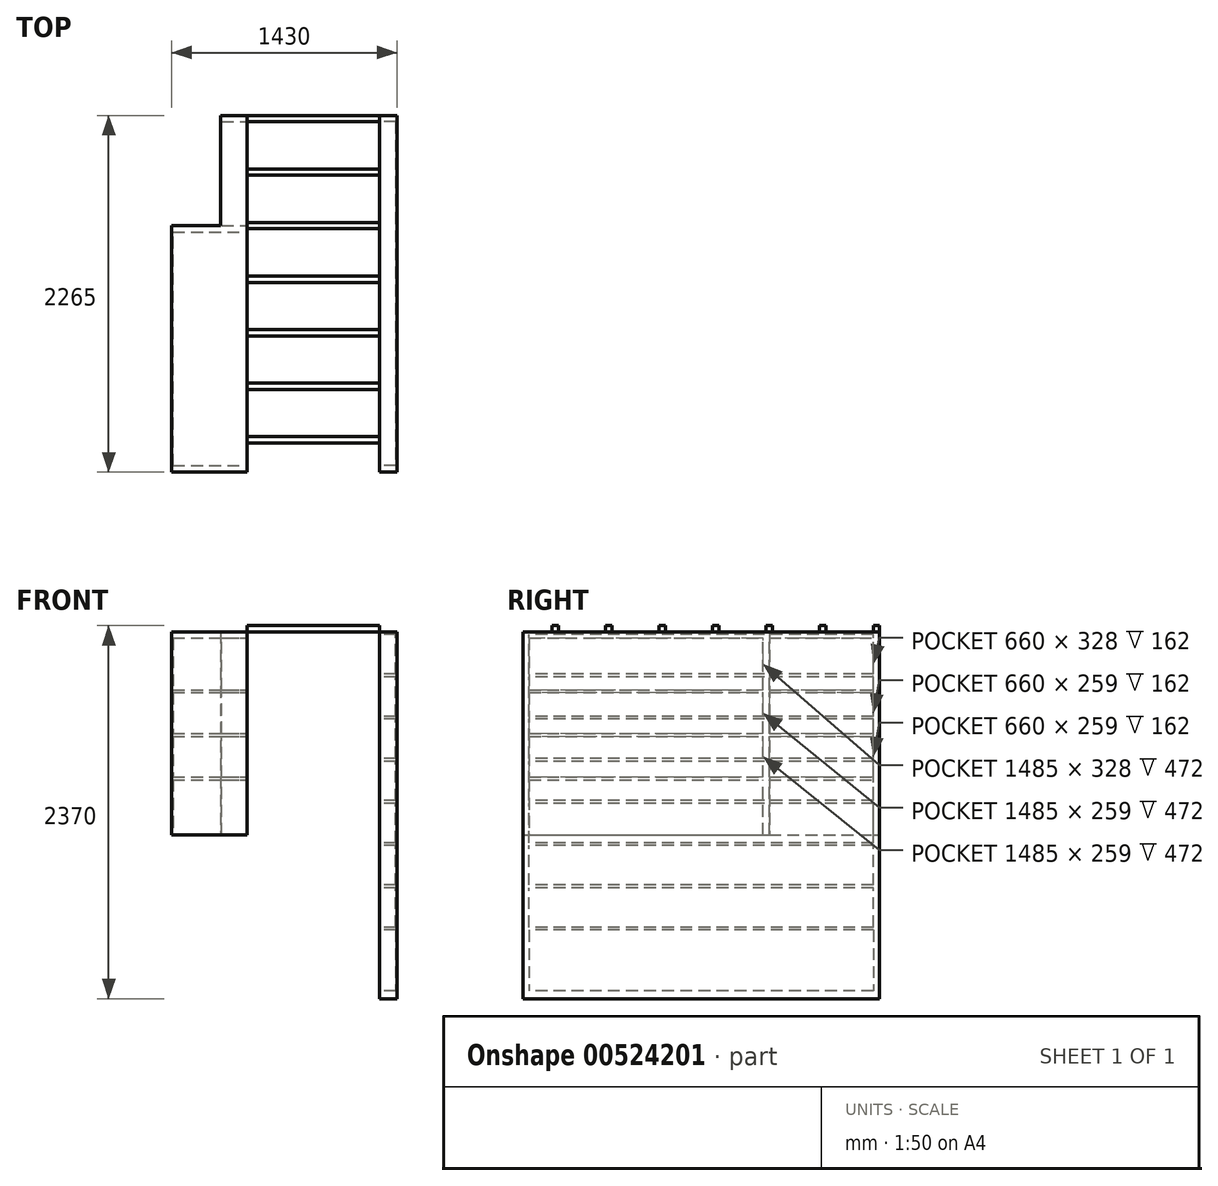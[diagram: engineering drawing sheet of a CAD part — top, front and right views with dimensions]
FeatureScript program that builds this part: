
annotation { "Feature Type Name" : "Feature", "Feature Type Description" : "" }
export const myFeature = defineFeature(function(context is Context, id is Id, definition is map)
    precondition{}
    {
        {
            var Q0;
            Q0=qCreatedBy(makeId("Top.planeOp"),FACE);
            var sketch = newSketch(context, id + "F0", { "sketchPlane" : qUnion([Q0])});
            skLineSegment(sketch, "E0.bottom", {"start": v(0, 0) * mm, "end": v(-110, 0) * mm});
            skLineSegment(sketch, "E0.left", {"start": v(0, 0) * mm, "end": v(0, 789.64) * mm});
            skLineSegment(sketch, "E0.right", {"start": v(-110, 0) * mm, "end": v(-110, 789.64) * mm});
            skLineSegment(sketch, "E1.bottom", {"start": v(-1120, 2265) * mm, "end": v(-950, 2265) * mm});
            skLineSegment(sketch, "E1.top", {"start": v(-1120, 0) * mm, "end": v(-950, 0) * mm});
            skLineSegment(sketch, "E1.left", {"start": v(-1120, 2265) * mm, "end": v(-1120, 1565) * mm});
            skLineSegment(sketch, "E1.right", {"start": v(-950, 2265) * mm, "end": v(-950, 0) * mm});
            skLineSegment(sketch, "E2.bottom", {"start": v(-1120, 1565) * mm, "end": v(-1430, 1565) * mm});
            skLineSegment(sketch, "E2.top", {"start": v(-950, 0) * mm, "end": v(-1430, 0) * mm});
            skLineSegment(sketch, "E2.right", {"start": v(-1430, 1565) * mm, "end": v(-1430, 0) * mm});
            skLineSegment(sketch, "E3.bottom", {"start": v(-110, 2265) * mm, "end": v(0, 2265) * mm});
            skLineSegment(sketch, "E3.top", {"start": v(-110, 0) * mm, "end": v(0, 0) * mm});
            skLineSegment(sketch, "E3.left", {"start": v(-110, 2265) * mm, "end": v(-110, 0) * mm});
            skLineSegment(sketch, "E3.right", {"start": v(0, 2265) * mm, "end": v(0, 0) * mm});
            skSolve(sketch);
        }
        {
            var Q0;
            Q0 = qSketchRegion(id + "F0", true);
            extrude(context, id + "F1", {"entities" : qUnion([Q0]), "depth" : 2330 * mm, "offsetDistance" : 25 * mm});
        }
        {
            var Q0;
            Q0=makeQuery(id+"F1.opExtrude","SWEPT_FACE",FACE,{"disambiguationData":[OSD([sQuery(id+"F0.wireOp",EDGE,"E3.left")])]});
            var sketch = newSketch(context, id + "F2", { "sketchPlane" : qUnion([Q0])});
            skLineSegment(sketch, "E4.0", {"start": v(-2265, 2330) * mm, "end": v(-2265, 0) * mm});
            skLineSegment(sketch, "E5.0", {"start": v(0, 2330) * mm, "end": v(0, 0) * mm});
            skLineSegment(sketch, "E6.0", {"start": v(-2265, 2330) * mm, "end": v(0, 2330) * mm});
            skLineSegment(sketch, "E7.0", {"start": v(-2265, 0) * mm, "end": v(0, 0) * mm});
            skLineSegment(sketch, "E8.bottom", {"start": v(-2225, 436) * mm, "end": v(-40, 436) * mm});
            skLineSegment(sketch, "E8.top", {"start": v(-2225, 50) * mm, "end": v(-40, 50) * mm});
            skLineSegment(sketch, "E8.left", {"start": v(-2225, 436) * mm, "end": v(-2225, 50) * mm});
            skLineSegment(sketch, "E8.right", {"start": v(-40, 436) * mm, "end": v(-40, 50) * mm});
            skLineSegment(sketch, "E9.bottom", {"start": v(-2225, 454) * mm, "end": v(-40, 454) * mm});
            skLineSegment(sketch, "E9.top", {"start": v(-2225, 704) * mm, "end": v(-40, 704) * mm});
            skLineSegment(sketch, "E9.left", {"start": v(-2225, 454) * mm, "end": v(-2225, 704) * mm});
            skLineSegment(sketch, "E9.right", {"start": v(-40, 454) * mm, "end": v(-40, 704) * mm});
            skLineSegment(sketch, "E10.bottom", {"start": v(-2225, 722) * mm, "end": v(-40, 722) * mm});
            skLineSegment(sketch, "E10.top", {"start": v(-2225, 972) * mm, "end": v(-40, 972) * mm});
            skLineSegment(sketch, "E10.left", {"start": v(-2225, 722) * mm, "end": v(-2225, 972) * mm});
            skLineSegment(sketch, "E10.right", {"start": v(-40, 722) * mm, "end": v(-40, 972) * mm});
            skLineSegment(sketch, "E11.bottom", {"start": v(-2225, 990) * mm, "end": v(-40, 990) * mm});
            skLineSegment(sketch, "E11.top", {"start": v(-2225, 1240) * mm, "end": v(-40, 1240) * mm});
            skLineSegment(sketch, "E11.left", {"start": v(-2225, 990) * mm, "end": v(-2225, 1240) * mm});
            skLineSegment(sketch, "E11.right", {"start": v(-40, 990) * mm, "end": v(-40, 1240) * mm});
            skLineSegment(sketch, "E12.bottom", {"start": v(-2225, 1258) * mm, "end": v(-40, 1258) * mm});
            skLineSegment(sketch, "E12.top", {"start": v(-2225, 1508) * mm, "end": v(-40, 1508) * mm});
            skLineSegment(sketch, "E12.left", {"start": v(-2225, 1258) * mm, "end": v(-2225, 1508) * mm});
            skLineSegment(sketch, "E12.right", {"start": v(-40, 1258) * mm, "end": v(-40, 1508) * mm});
            skLineSegment(sketch, "E13.bottom", {"start": v(-2225, 1526) * mm, "end": v(-40, 1526) * mm});
            skLineSegment(sketch, "E13.top", {"start": v(-2225, 1776) * mm, "end": v(-40, 1776) * mm});
            skLineSegment(sketch, "E13.left", {"start": v(-2225, 1526) * mm, "end": v(-2225, 1776) * mm});
            skLineSegment(sketch, "E13.right", {"start": v(-40, 1526) * mm, "end": v(-40, 1776) * mm});
            skLineSegment(sketch, "E14.bottom", {"start": v(-2225, 1794) * mm, "end": v(-40, 1794) * mm});
            skLineSegment(sketch, "E14.top", {"start": v(-2225, 2044) * mm, "end": v(-40, 2044) * mm});
            skLineSegment(sketch, "E14.left", {"start": v(-2225, 1794) * mm, "end": v(-2225, 2044) * mm});
            skLineSegment(sketch, "E14.right", {"start": v(-40, 1794) * mm, "end": v(-40, 2044) * mm});
            skLineSegment(sketch, "E15.bottom", {"start": v(-2225, 2062) * mm, "end": v(-40, 2062) * mm});
            skLineSegment(sketch, "E15.top", {"start": v(-2225, 2312) * mm, "end": v(-40, 2312) * mm});
            skLineSegment(sketch, "E15.left", {"start": v(-2225, 2062) * mm, "end": v(-2225, 2312) * mm});
            skLineSegment(sketch, "E15.right", {"start": v(-40, 2062) * mm, "end": v(-40, 2312) * mm});
            skSolve(sketch);
        }
        {
            var Q0;
            Q0=makeQuery(id+"F2.imprint","IMPRINT",FACE,{"disambiguationData":[TD([[makeQuery(id+"F2.imprint","IMPRINT",EDGE,{"derivedFrom":sQuery(id+"F2.wireOp",EDGE,"E15.bottom")}),1.0]])]});
            var Q1;
            Q1=makeQuery(id+"F2.imprint","IMPRINT",FACE,{"disambiguationData":[TD([[makeQuery(id+"F2.imprint","IMPRINT",EDGE,{"derivedFrom":sQuery(id+"F2.wireOp",EDGE,"E14.bottom")}),1.0]])]});
            var Q2;
            Q2=makeQuery(id+"F2.imprint","IMPRINT",FACE,{"disambiguationData":[TD([[makeQuery(id+"F2.imprint","IMPRINT",EDGE,{"derivedFrom":sQuery(id+"F2.wireOp",EDGE,"E13.bottom")}),1.0]])]});
            var Q3;
            Q3=makeQuery(id+"F2.imprint","IMPRINT",FACE,{"disambiguationData":[TD([[makeQuery(id+"F2.imprint","IMPRINT",EDGE,{"derivedFrom":sQuery(id+"F2.wireOp",EDGE,"E12.bottom")}),1.0]])]});
            var Q4;
            Q4=makeQuery(id+"F2.imprint","IMPRINT",FACE,{"disambiguationData":[TD([[makeQuery(id+"F2.imprint","IMPRINT",EDGE,{"derivedFrom":sQuery(id+"F2.wireOp",EDGE,"E11.bottom")}),1.0]])]});
            var Q5;
            Q5=makeQuery(id+"F2.imprint","IMPRINT",FACE,{"disambiguationData":[TD([[makeQuery(id+"F2.imprint","IMPRINT",EDGE,{"derivedFrom":sQuery(id+"F2.wireOp",EDGE,"E10.bottom")}),1.0]])]});
            var Q6;
            Q6=makeQuery(id+"F2.imprint","IMPRINT",FACE,{"disambiguationData":[TD([[makeQuery(id+"F2.imprint","IMPRINT",EDGE,{"derivedFrom":sQuery(id+"F2.wireOp",EDGE,"E9.bottom")}),1.0]])]});
            var Q7;
            Q7=makeQuery(id+"F2.imprint","IMPRINT",FACE,{"disambiguationData":[TD([[makeQuery(id+"F2.imprint","IMPRINT",EDGE,{"derivedFrom":sQuery(id+"F2.wireOp",EDGE,"E8.bottom")}),-1.0]])]});
            extrude(context, id + "F3", {"entities" : qUnion([Q0, Q1, Q2, Q3, Q4, Q5, Q6, Q7]), "operationType" : NewBodyOperationType.REMOVE, "oppositeDirection" : true, "depth" : 102 * mm, "offsetDistance" : 25 * mm});
        }
        {
            var Q0;
            Q0=makeQuery(id+"F1.opExtrude","SWEPT_FACE",FACE,{"disambiguationData":[OSD([sQuery(id+"F0.wireOp",EDGE,"E1.right")])]});
            var sketch = newSketch(context, id + "F4", { "sketchPlane" : qUnion([Q0])});
            skLineSegment(sketch, "E16.0", {"start": v(0, 2330) * mm, "end": v(0, 0) * mm});
            skLineSegment(sketch, "E17.0.1", {"start": v(0, 0) * mm, "end": v(1565, 0) * mm});
            skLineSegment(sketch, "E17.0.3", {"start": v(1565, 0) * mm, "end": v(2265, 0) * mm});
            skLineSegment(sketch, "E17.0.5", {"start": v(2265, 0) * mm, "end": v(0, 0) * mm});
            skLineSegment(sketch, "E18.0", {"start": v(2265, 2330) * mm, "end": v(2265, 0) * mm});
            skLineSegment(sketch, "E19.bottom", {"start": v(0, 0) * mm, "end": v(2265, 0) * mm});
            skLineSegment(sketch, "E19.top", {"start": v(0, 1040) * mm, "end": v(2265, 1040) * mm});
            skLineSegment(sketch, "E19.left", {"start": v(0, 0) * mm, "end": v(0, 1040) * mm});
            skLineSegment(sketch, "E19.right", {"start": v(2265, 0) * mm, "end": v(2265, 1040) * mm});
            skSolve(sketch);
        }
        {
            var Q0;
            Q0 = qSketchRegion(id + "F4", true);
            extrude(context, id + "F5", {"entities" : qUnion([Q0]), "operationType" : NewBodyOperationType.REMOVE, "oppositeDirection" : true, "depth" : 480 * mm, "offsetDistance" : 25 * mm});
        }
        {
            var Q0;
            Q0=makeQuery(id+"F1.opExtrude","SWEPT_FACE",FACE,{"disambiguationData":[OSD([sQuery(id+"F0.wireOp",EDGE,"E1.right")])]});
            var sketch = newSketch(context, id + "F6", { "sketchPlane" : qUnion([Q0])});
            skLineSegment(sketch, "E20.0", {"start": v(0, 2330) * mm, "end": v(0, 1040) * mm});
            skLineSegment(sketch, "E21.0", {"start": v(0, 1040) * mm, "end": v(2265, 1040) * mm});
            skLineSegment(sketch, "E22.0", {"start": v(2265, 2330) * mm, "end": v(2265, 1040) * mm});
            skLineSegment(sketch, "E23.bottom", {"start": v(2265, 1040) * mm, "end": v(2225, 1040) * mm});
            skLineSegment(sketch, "E23.top", {"start": v(2265, 2330) * mm, "end": v(2225, 2330) * mm});
            skLineSegment(sketch, "E23.left", {"start": v(2265, 1040) * mm, "end": v(2265, 2330) * mm});
            skLineSegment(sketch, "E23.right", {"start": v(2225, 1040) * mm, "end": v(2225, 2330) * mm});
            skLineSegment(sketch, "E24.bottom", {"start": v(0, 2290) * mm, "end": v(2225, 2290) * mm});
            skLineSegment(sketch, "E24.top", {"start": v(0, 2330) * mm, "end": v(2225, 2330) * mm});
            skLineSegment(sketch, "E24.left", {"start": v(0, 2290) * mm, "end": v(0, 2330) * mm});
            skLineSegment(sketch, "E24.right", {"start": v(2225, 2290) * mm, "end": v(2225, 2330) * mm});
            skLineSegment(sketch, "E25.bottom", {"start": v(0, 2290) * mm, "end": v(40, 2290) * mm});
            skLineSegment(sketch, "E25.top", {"start": v(0, 1040) * mm, "end": v(40, 1040) * mm});
            skLineSegment(sketch, "E25.left", {"start": v(0, 2290) * mm, "end": v(0, 1040) * mm});
            skLineSegment(sketch, "E25.right", {"start": v(40, 2290) * mm, "end": v(40, 1040) * mm});
            skLineSegment(sketch, "E26.bottom", {"start": v(1565, 1040) * mm, "end": v(1525, 1040) * mm});
            skLineSegment(sketch, "E26.top", {"start": v(1565, 2290) * mm, "end": v(1525, 2290) * mm});
            skLineSegment(sketch, "E26.left", {"start": v(1565, 1040) * mm, "end": v(1565, 2290) * mm});
            skLineSegment(sketch, "E26.right", {"start": v(1525, 1040) * mm, "end": v(1525, 2290) * mm});
            skLineSegment(sketch, "E27.bottom", {"start": v(40, 1390) * mm, "end": v(2225, 1390) * mm});
            skLineSegment(sketch, "E27.top", {"start": v(40, 1408) * mm, "end": v(2225, 1408) * mm});
            skLineSegment(sketch, "E27.left", {"start": v(40, 1390) * mm, "end": v(40, 1408) * mm});
            skLineSegment(sketch, "E27.right", {"start": v(2225, 1390) * mm, "end": v(2225, 1408) * mm});
            skLineSegment(sketch, "E28.bottom", {"start": v(40, 1667) * mm, "end": v(2225, 1667) * mm});
            skLineSegment(sketch, "E28.top", {"start": v(40, 1685) * mm, "end": v(2225, 1685) * mm});
            skLineSegment(sketch, "E28.left", {"start": v(40, 1667) * mm, "end": v(40, 1685) * mm});
            skLineSegment(sketch, "E28.right", {"start": v(2225, 1667) * mm, "end": v(2225, 1685) * mm});
            skLineSegment(sketch, "E29.bottom", {"start": v(40, 1944) * mm, "end": v(2225, 1944) * mm});
            skLineSegment(sketch, "E29.top", {"start": v(40, 1962) * mm, "end": v(2225, 1962) * mm});
            skLineSegment(sketch, "E29.left", {"start": v(40, 1944) * mm, "end": v(40, 1962) * mm});
            skLineSegment(sketch, "E29.right", {"start": v(2225, 1944) * mm, "end": v(2225, 1962) * mm});
            skSolve(sketch);
        }
        {
            var Q0;
            {var subQ3=sQuery(id+"F6.wireOp",EDGE,"E26.left");var subQ5=sQuery(id+"F6.wireOp",EDGE,"E27.bottom");var subQ7=makeQuery(id+"F6.imprint","INTERSECT",VERTEX,{"derivedFrom":[subQ3,subQ5]});Q0=makeQuery(id+"F6.imprint","IMPRINT",FACE,{"disambiguationData":[TD([[makeQuery(id+"F6.imprint","IMPRINT",EDGE,{"disambiguationData":[TD([[subQ7,1.0]])],"derivedFrom":subQ3}),-1.0]])]});}
            var Q1;
            {var subQ0=sQuery(id+"F6.wireOp",EDGE,"E27.top");var subQ5=sQuery(id+"F6.wireOp",EDGE,"E26.left");var subQ6=makeQuery(id+"F6.imprint","INTERSECT",VERTEX,{"derivedFrom":[subQ5,subQ0]});Q1=makeQuery(id+"F6.imprint","IMPRINT",FACE,{"disambiguationData":[TD([[makeQuery(id+"F6.imprint","IMPRINT",EDGE,{"disambiguationData":[TD([[subQ6,-1.0]])],"derivedFrom":subQ5}),-1.0]])]});}
            var Q2;
            {var subQ0=sQuery(id+"F6.wireOp",EDGE,"E28.top");var subQ5=sQuery(id+"F6.wireOp",EDGE,"E26.left");var subQ6=makeQuery(id+"F6.imprint","INTERSECT",VERTEX,{"derivedFrom":[subQ5,subQ0]});Q2=makeQuery(id+"F6.imprint","IMPRINT",FACE,{"disambiguationData":[TD([[makeQuery(id+"F6.imprint","IMPRINT",EDGE,{"disambiguationData":[TD([[subQ6,-1.0]])],"derivedFrom":subQ5}),-1.0]])]});}
            var Q3;
            {var subQ3=sQuery(id+"F6.wireOp",EDGE,"E29.top");var subQ5=sQuery(id+"F6.wireOp",EDGE,"E26.left");var subQ6=makeQuery(id+"F6.imprint","INTERSECT",VERTEX,{"derivedFrom":[subQ5,subQ3]});Q3=makeQuery(id+"F6.imprint","IMPRINT",FACE,{"disambiguationData":[TD([[makeQuery(id+"F6.imprint","IMPRINT",EDGE,{"disambiguationData":[TD([[subQ6,-1.0]])],"derivedFrom":subQ5}),-1.0]])]});}
            extrude(context, id + "F7", {"entities" : qUnion([Q0, Q1, Q2, Q3]), "operationType" : NewBodyOperationType.REMOVE, "oppositeDirection" : true, "depth" : 162 * mm, "offsetDistance" : 25 * mm});
        }
        {
            var Q0;
            {var subQ3=sQuery(id+"F6.wireOp",EDGE,"E26.right");var subQ5=sQuery(id+"F6.wireOp",EDGE,"E27.bottom");var subQ7=makeQuery(id+"F6.imprint","INTERSECT",VERTEX,{"derivedFrom":[subQ3,subQ5]});Q0=makeQuery(id+"F6.imprint","IMPRINT",FACE,{"disambiguationData":[TD([[makeQuery(id+"F6.imprint","IMPRINT",EDGE,{"disambiguationData":[TD([[subQ7,1.0]])],"derivedFrom":subQ3}),1.0]])]});}
            var Q1;
            {var subQ0=sQuery(id+"F6.wireOp",EDGE,"E27.top");var subQ5=sQuery(id+"F6.wireOp",EDGE,"E26.right");var subQ6=makeQuery(id+"F6.imprint","INTERSECT",VERTEX,{"derivedFrom":[subQ5,subQ0]});Q1=makeQuery(id+"F6.imprint","IMPRINT",FACE,{"disambiguationData":[TD([[makeQuery(id+"F6.imprint","IMPRINT",EDGE,{"disambiguationData":[TD([[subQ6,-1.0]])],"derivedFrom":subQ5}),1.0]])]});}
            var Q2;
            {var subQ0=sQuery(id+"F6.wireOp",EDGE,"E28.top");var subQ5=sQuery(id+"F6.wireOp",EDGE,"E26.right");var subQ6=makeQuery(id+"F6.imprint","INTERSECT",VERTEX,{"derivedFrom":[subQ5,subQ0]});Q2=makeQuery(id+"F6.imprint","IMPRINT",FACE,{"disambiguationData":[TD([[makeQuery(id+"F6.imprint","IMPRINT",EDGE,{"disambiguationData":[TD([[subQ6,-1.0]])],"derivedFrom":subQ5}),1.0]])]});}
            var Q3;
            {var subQ3=sQuery(id+"F6.wireOp",EDGE,"E26.right");var subQ5=sQuery(id+"F6.wireOp",EDGE,"E29.top");var subQ7=makeQuery(id+"F6.imprint","INTERSECT",VERTEX,{"derivedFrom":[subQ3,subQ5]});Q3=makeQuery(id+"F6.imprint","IMPRINT",FACE,{"disambiguationData":[TD([[makeQuery(id+"F6.imprint","IMPRINT",EDGE,{"disambiguationData":[TD([[subQ7,-1.0]])],"derivedFrom":subQ3}),1.0]])]});}
            extrude(context, id + "F8", {"entities" : qUnion([Q0, Q1, Q2, Q3]), "operationType" : NewBodyOperationType.REMOVE, "oppositeDirection" : true, "depth" : 472 * mm, "offsetDistance" : 25 * mm});
        }
        {
            var Q0;
            Q0=makeQuery(id+"F1.opExtrude","CAP_FACE",FACE,{"disambiguationData":[OSD([sQuery(id+"F0.wireOp",EDGE,"E1.bottom"),sQuery(id+"F0.wireOp",EDGE,"E1.left"),sQuery(id+"F0.wireOp",EDGE,"E1.right"),sQuery(id+"F0.wireOp",EDGE,"E2.bottom"),sQuery(id+"F0.wireOp",EDGE,"E2.top"),sQuery(id+"F0.wireOp",EDGE,"E2.right")])],"isStart":false});
            var sketch = newSketch(context, id + "F9", { "sketchPlane" : qUnion([Q0])});
            skLineSegment(sketch, "E30.0", {"start": v(-950, 0) * mm, "end": v(-950, 2225) * mm});
            skLineSegment(sketch, "E31.0.0", {"start": v(-110, 2265) * mm, "end": v(-110, 0) * mm});
            skLineSegment(sketch, "E31.0.1", {"start": v(-110, 0) * mm, "end": v(0, 0) * mm});
            skLineSegment(sketch, "E31.0.2", {"start": v(0, 0) * mm, "end": v(0, 2265) * mm});
            skLineSegment(sketch, "E31.0.3", {"start": v(0, 2265) * mm, "end": v(-110, 2265) * mm});
            skLineSegment(sketch, "E32.0", {"start": v(-950, 0) * mm, "end": v(-1430, 0) * mm});
            skLineSegment(sketch, "E33.0", {"start": v(-950, 2265) * mm, "end": v(-950, 2225) * mm});
            skLineSegment(sketch, "E34.0", {"start": v(-1120, 2265) * mm, "end": v(-950, 2265) * mm});
            skLineSegment(sketch, "E35.bottom", {"start": v(-950, 565) * mm, "end": v(-110, 565) * mm});
            skLineSegment(sketch, "E35.top", {"start": v(-950, 525) * mm, "end": v(-110, 525) * mm});
            skLineSegment(sketch, "E35.left", {"start": v(-950, 565) * mm, "end": v(-950, 525) * mm});
            skLineSegment(sketch, "E35.right", {"start": v(-110, 565) * mm, "end": v(-110, 525) * mm});
            skLineSegment(sketch, "E36.bottom", {"start": v(-950, 905) * mm, "end": v(-110, 905) * mm});
            skLineSegment(sketch, "E36.top", {"start": v(-950, 865) * mm, "end": v(-110, 865) * mm});
            skLineSegment(sketch, "E36.left", {"start": v(-950, 905) * mm, "end": v(-950, 865) * mm});
            skLineSegment(sketch, "E36.right", {"start": v(-110, 905) * mm, "end": v(-110, 865) * mm});
            skLineSegment(sketch, "E37.bottom", {"start": v(-950, 1245) * mm, "end": v(-110, 1245) * mm});
            skLineSegment(sketch, "E37.top", {"start": v(-950, 1205) * mm, "end": v(-110, 1205) * mm});
            skLineSegment(sketch, "E37.left", {"start": v(-950, 1245) * mm, "end": v(-950, 1205) * mm});
            skLineSegment(sketch, "E37.right", {"start": v(-110, 1245) * mm, "end": v(-110, 1205) * mm});
            skLineSegment(sketch, "E38.bottom", {"start": v(-950, 1545) * mm, "end": v(-110, 1545) * mm});
            skLineSegment(sketch, "E38.top", {"start": v(-950, 1585) * mm, "end": v(-110, 1585) * mm});
            skLineSegment(sketch, "E38.left", {"start": v(-950, 1545) * mm, "end": v(-950, 1585) * mm});
            skLineSegment(sketch, "E38.right", {"start": v(-110, 1545) * mm, "end": v(-110, 1585) * mm});
            skLineSegment(sketch, "E39.bottom", {"start": v(-950, 1885) * mm, "end": v(-110, 1885) * mm});
            skLineSegment(sketch, "E39.top", {"start": v(-950, 1925) * mm, "end": v(-110, 1925) * mm});
            skLineSegment(sketch, "E39.left", {"start": v(-950, 1885) * mm, "end": v(-950, 1925) * mm});
            skLineSegment(sketch, "E39.right", {"start": v(-110, 1885) * mm, "end": v(-110, 1925) * mm});
            skLineSegment(sketch, "E40.bottom", {"start": v(-950, 2225) * mm, "end": v(-110, 2225) * mm});
            skLineSegment(sketch, "E40.top", {"start": v(-950, 2265) * mm, "end": v(-110, 2265) * mm});
            skLineSegment(sketch, "E40.left", {"start": v(-950, 2225) * mm, "end": v(-950, 2265) * mm});
            skLineSegment(sketch, "E40.right", {"start": v(-110, 2225) * mm, "end": v(-110, 2265) * mm});
            skLineSegment(sketch, "E41.bottom", {"start": v(-950, 0) * mm, "end": v(-110, 0) * mm});
            skLineSegment(sketch, "E41.top", {"start": v(-950, 225) * mm, "end": v(-110, 225) * mm});
            skLineSegment(sketch, "E41.left", {"start": v(-950, 0) * mm, "end": v(-950, 225) * mm});
            skLineSegment(sketch, "E41.right", {"start": v(-110, 0) * mm, "end": v(-110, 225) * mm});
            skLineSegment(sketch, "E42.top", {"start": v(-950, 185) * mm, "end": v(-110, 185) * mm});
            skLineSegment(sketch, "E42.left", {"start": v(-950, 225) * mm, "end": v(-950, 185) * mm});
            skLineSegment(sketch, "E42.right", {"start": v(-110, 225) * mm, "end": v(-110, 185) * mm});
            skLineSegment(sketch, "E43.bottom", {"start": v(-950, 2265) * mm, "end": v(-990, 2265) * mm});
            skLineSegment(sketch, "E43.top", {"start": v(-950, 185) * mm, "end": v(-990, 185) * mm});
            skLineSegment(sketch, "E43.left", {"start": v(-950, 2265) * mm, "end": v(-950, 185) * mm});
            skLineSegment(sketch, "E43.right", {"start": v(-990, 2265) * mm, "end": v(-990, 185) * mm});
            skLineSegment(sketch, "E44.bottom", {"start": v(-110, 2265) * mm, "end": v(-70, 2265) * mm});
            skLineSegment(sketch, "E44.top", {"start": v(-110, 185) * mm, "end": v(-70, 185) * mm});
            skLineSegment(sketch, "E44.left", {"start": v(-110, 2265) * mm, "end": v(-110, 185) * mm});
            skLineSegment(sketch, "E44.right", {"start": v(-70, 2265) * mm, "end": v(-70, 185) * mm});
            skSolve(sketch);
        }
        {
            var Q0;
            {var subQ0=sQuery(id+"F9.wireOp",EDGE,"E39.bottom");Q0=makeQuery(id+"F9.imprint","IMPRINT",FACE,{"disambiguationData":[TD([[makeQuery(id+"F9.imprint","IMPRINT",EDGE,{"derivedFrom":subQ0}),1.0]])]});}
            var Q1;
            {var subQ0=sQuery(id+"F9.wireOp",EDGE,"E38.bottom");Q1=makeQuery(id+"F9.imprint","IMPRINT",FACE,{"disambiguationData":[TD([[makeQuery(id+"F9.imprint","IMPRINT",EDGE,{"derivedFrom":subQ0}),1.0]])]});}
            var Q2;
            {var subQ0=sQuery(id+"F9.wireOp",EDGE,"E37.bottom");Q2=makeQuery(id+"F9.imprint","IMPRINT",FACE,{"disambiguationData":[TD([[makeQuery(id+"F9.imprint","IMPRINT",EDGE,{"derivedFrom":subQ0}),-1.0]])]});}
            var Q3;
            {var subQ0=sQuery(id+"F9.wireOp",EDGE,"E36.bottom");Q3=makeQuery(id+"F9.imprint","IMPRINT",FACE,{"disambiguationData":[TD([[makeQuery(id+"F9.imprint","IMPRINT",EDGE,{"derivedFrom":subQ0}),-1.0]])]});}
            var Q4;
            {var subQ0=sQuery(id+"F9.wireOp",EDGE,"E41.top");Q4=makeQuery(id+"F9.imprint","IMPRINT",FACE,{"disambiguationData":[TD([[makeQuery(id+"F9.imprint","IMPRINT",EDGE,{"derivedFrom":subQ0}),-1.0]])]});}
            var Q5;
            {var subQ0=sQuery(id+"F9.wireOp",EDGE,"E35.bottom");Q5=makeQuery(id+"F9.imprint","IMPRINT",FACE,{"disambiguationData":[TD([[makeQuery(id+"F9.imprint","IMPRINT",EDGE,{"derivedFrom":subQ0}),-1.0]])]});}
            var Q6;
            {var subQ8=sQuery(id+"F9.wireOp",EDGE,"E44.bottom");Q6=makeQuery(id+"F9.imprint","IMPRINT",FACE,{"disambiguationData":[TD([[makeQuery(id+"F9.imprint","IMPRINT",EDGE,{"derivedFrom":subQ8}),-1.0]])]});}
            var Q7;
            {var subQ8=sQuery(id+"F9.wireOp",EDGE,"E43.bottom");Q7=makeQuery(id+"F9.imprint","IMPRINT",FACE,{"disambiguationData":[TD([[makeQuery(id+"F9.imprint","IMPRINT",EDGE,{"derivedFrom":subQ8}),-1.0]])]});}
            var Q8;
            {var subQ0=sQuery(id+"F9.wireOp",EDGE,"E40.bottom");Q8=makeQuery(id+"F9.imprint","IMPRINT",FACE,{"disambiguationData":[TD([[makeQuery(id+"F9.imprint","IMPRINT",EDGE,{"derivedFrom":subQ0}),1.0]])]});}
            extrude(context, id + "F10", {"entities" : qUnion([Q0, Q1, Q2, Q3, Q4, Q5, Q6, Q7, Q8]), "depth" : 40 * mm, "offsetDistance" : 25 * mm});
        }
    });
